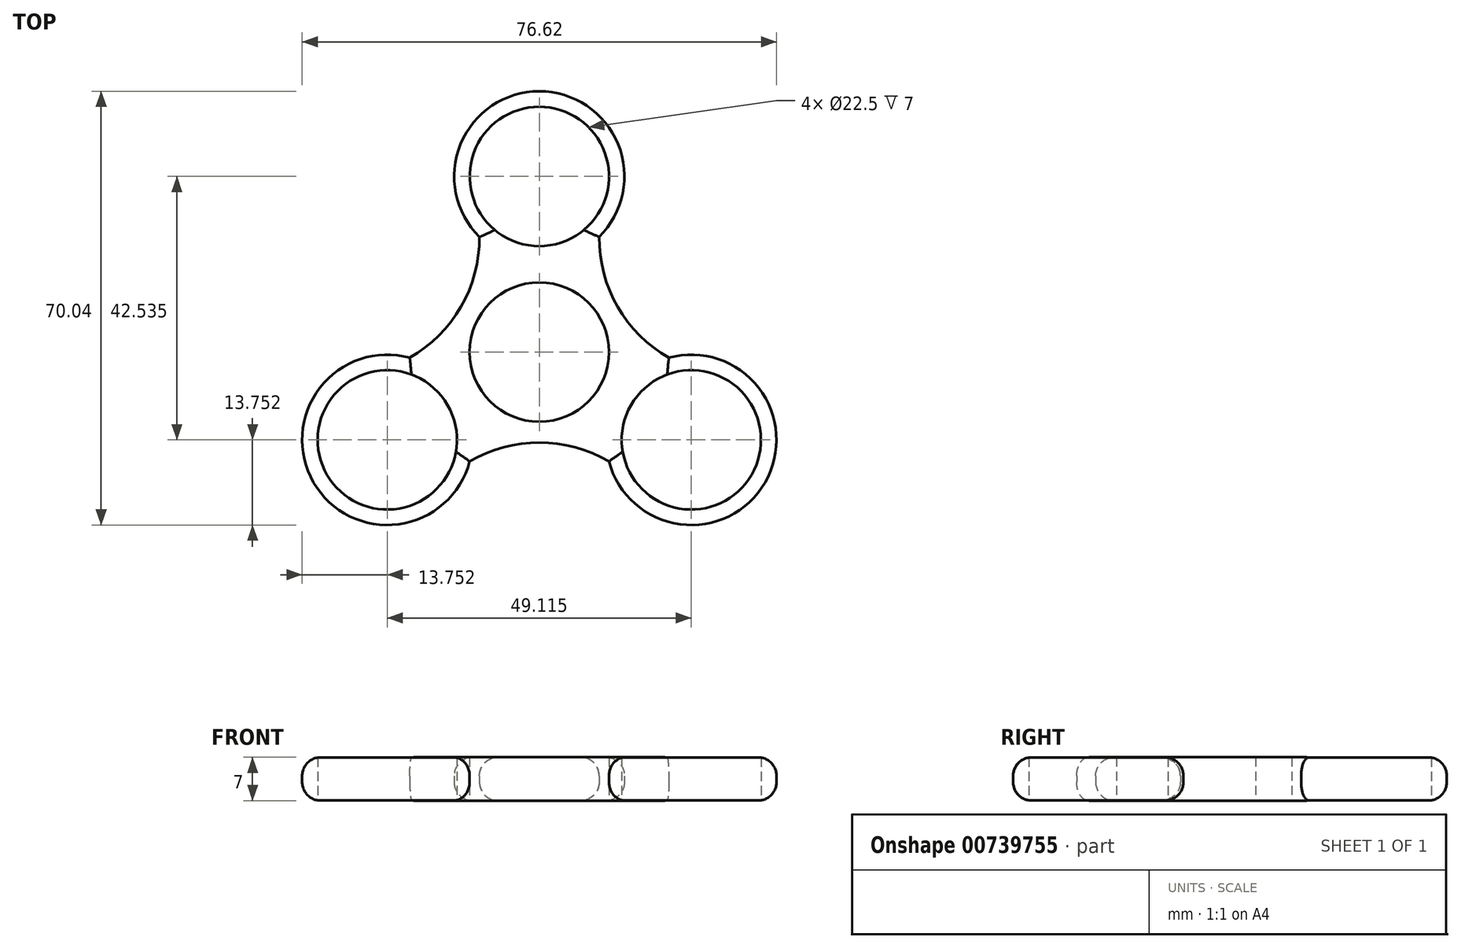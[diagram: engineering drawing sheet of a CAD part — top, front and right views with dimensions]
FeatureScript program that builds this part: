
annotation { "Feature Type Name" : "Feature", "Feature Type Description" : "" }
export const myFeature = defineFeature(function(context is Context, id is Id, definition is map)
    precondition{}
    {
        {
            var Q0;
            Q0=qCreatedBy(makeId("Top.planeOp"),FACE);
            var sketch = newSketch(context, id + "F0", { "sketchPlane" : qUnion([Q0])});
            skCircle(sketch, "E0", {"center": v(0, 0) * mm, "radius": 11.25 * mm});
            skCircle(sketch, "E1", {"center": v(0, 28.36) * mm, "radius": 11.25 * mm});
            skCircle(sketch, "E2.1.0", {"center": v(-24.56, -14.18) * mm, "radius": 11.25 * mm});
            skCircle(sketch, "E2.2.0", {"center": v(24.56, -14.18) * mm, "radius": 11.25 * mm});
            skArc(sketch, "E3", {"start": v(-20.93, -0.91) * mm, "mid": v(-36.47, -21.05) * mm, "end": v(-11.26, -17.67) * mm});
            skArc(sketch, "E4", {"start": v(9.67, 18.59) * mm, "mid": v(0, 42.1) * mm, "end": v(-9.67, 18.59) * mm});
            skArc(sketch, "E5", {"start": v(11.26, -17.67) * mm, "mid": v(36.47, -21.05) * mm, "end": v(20.93, -0.91) * mm});
            skArc(sketch, "E6.trimOffspring", {"start": v(26.02, -3.02) * mm, "mid": v(27.02, -3.28) * mm, "end": v(28.04, -3.48) * mm});
            skArc(sketch, "E7.trimOffspring", {"start": v(11.26, -17.67) * mm, "mid": v(0, -14.61) * mm, "end": v(-11.26, -17.67) * mm});
            skArc(sketch, "E8.trimOffspring", {"start": v(-20.93, -0.91) * mm, "mid": v(-12.66, 7.3) * mm, "end": v(-9.67, 18.59) * mm});
            skArc(sketch, "E9.trimOffspring", {"start": v(9.67, 18.59) * mm, "mid": v(12.66, 7.3) * mm, "end": v(20.93, -0.91) * mm});
            skSolve(sketch);
        }
        {
            var Q0;
            Q0 = qSketchRegion(id + "F0", true);
            extrude(context, id + "F1", {"entities" : qUnion([Q0]), "depth" : 7 * mm, "offsetDistance" : 25 * mm});
        }
        {
            var Q0;
            Q0=makeQuery(id+"F1.opExtrude","CAP_EDGE",EDGE,{"disambiguationData":[OSD([sQuery(id+"F0.wireOp",EDGE,"E5")])],"isStart":true});
            var Q1;
            Q1=makeQuery(id+"F1.opExtrude","CAP_EDGE",EDGE,{"disambiguationData":[OSD([sQuery(id+"F0.wireOp",EDGE,"E9.trimOffspring")])],"isStart":true});
            var Q2;
            Q2=makeQuery(id+"F1.opExtrude","CAP_EDGE",EDGE,{"disambiguationData":[OSD([sQuery(id+"F0.wireOp",EDGE,"E4")])],"isStart":true});
            var Q3;
            Q3=makeQuery(id+"F1.opExtrude","CAP_EDGE",EDGE,{"disambiguationData":[OSD([sQuery(id+"F0.wireOp",EDGE,"E8.trimOffspring")])],"isStart":true});
            var Q4;
            Q4=makeQuery(id+"F1.opExtrude","CAP_EDGE",EDGE,{"disambiguationData":[OSD([sQuery(id+"F0.wireOp",EDGE,"E3")])],"isStart":true});
            var Q5;
            Q5=makeQuery(id+"F1.opExtrude","CAP_EDGE",EDGE,{"disambiguationData":[OSD([sQuery(id+"F0.wireOp",EDGE,"E7.trimOffspring")])],"isStart":true});
            var Q6;
            Q6=makeQuery(id+"F1.opExtrude","CAP_EDGE",EDGE,{"disambiguationData":[OSD([sQuery(id+"F0.wireOp",EDGE,"E5")])],"isStart":false});
            var Q7;
            Q7=makeQuery(id+"F1.opExtrude","CAP_EDGE",EDGE,{"disambiguationData":[OSD([sQuery(id+"F0.wireOp",EDGE,"E7.trimOffspring")])],"isStart":false});
            var Q8;
            Q8=makeQuery(id+"F1.opExtrude","CAP_EDGE",EDGE,{"disambiguationData":[OSD([sQuery(id+"F0.wireOp",EDGE,"E3")])],"isStart":false});
            var Q9;
            Q9=makeQuery(id+"F1.opExtrude","CAP_EDGE",EDGE,{"disambiguationData":[OSD([sQuery(id+"F0.wireOp",EDGE,"E8.trimOffspring")])],"isStart":false});
            var Q10;
            Q10=makeQuery(id+"F1.opExtrude","CAP_EDGE",EDGE,{"disambiguationData":[OSD([sQuery(id+"F0.wireOp",EDGE,"E4")])],"isStart":false});
            var Q11;
            Q11=makeQuery(id+"F1.opExtrude","CAP_EDGE",EDGE,{"disambiguationData":[OSD([sQuery(id+"F0.wireOp",EDGE,"E9.trimOffspring")])],"isStart":false});
            fillet(context, id + "F2", {"entities" : qUnion([Q0, Q1, Q2, Q3, Q4, Q5, Q6, Q7, Q8, Q9, Q10, Q11]), "radius" : 3 * mm, "tangentPropagation" : true, "allowEdgeOverflow" : false});
        }
    });
